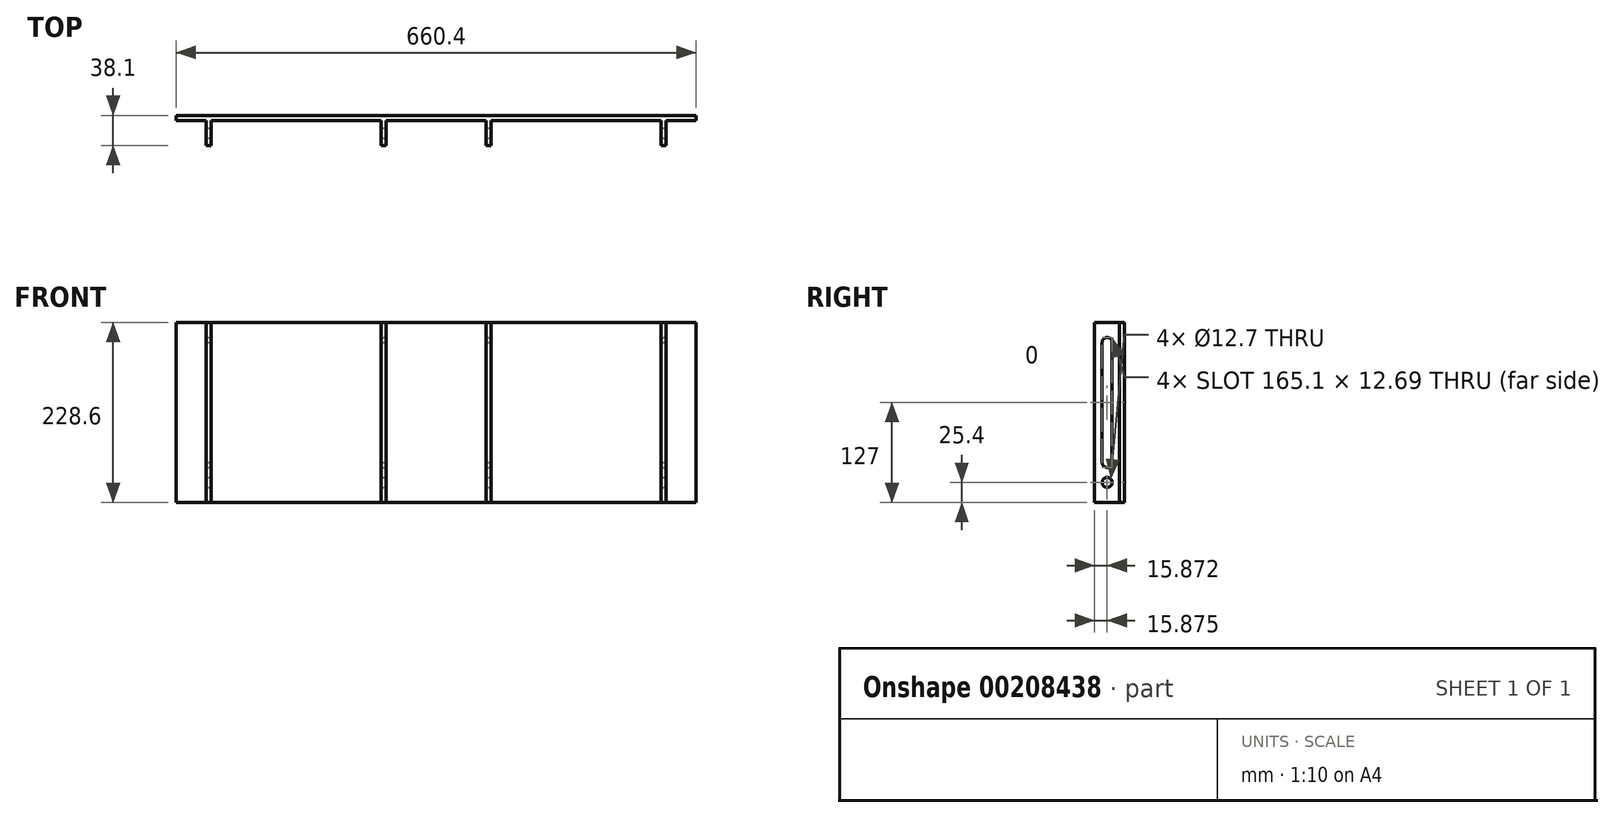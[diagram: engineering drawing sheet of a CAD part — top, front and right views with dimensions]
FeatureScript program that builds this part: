
annotation { "Feature Type Name" : "Feature", "Feature Type Description" : "" }
export const myFeature = defineFeature(function(context is Context, id is Id, definition is map)
    precondition{}
    {
        {
            var Q0;
            Q0=qCreatedBy(makeId("Front.planeOp"),FACE);
            var sketch = newSketch(context, id + "F0", { "sketchPlane" : qUnion([Q0])});
            skLineSegment(sketch, "E0.bottom", {"start": v(-330.2, 114.3) * mm, "end": v(330.2, 114.3) * mm});
            skLineSegment(sketch, "E0.top", {"start": v(-330.2, -114.3) * mm, "end": v(330.2, -114.3) * mm});
            skLineSegment(sketch, "E0.left", {"start": v(-330.2, 114.3) * mm, "end": v(-330.2, -114.3) * mm});
            skLineSegment(sketch, "E0.right", {"start": v(330.2, 114.3) * mm, "end": v(330.2, -114.3) * mm});
            skPoint(sketch, "E0.middle", {"position": v(0, 0) * mm});
            skLineSegment(sketch, "E1.bottom", {"start": v(-330.2, 114.3) * mm, "end": v(-292.1, 114.3) * mm});
            skLineSegment(sketch, "E1.top", {"start": v(-330.2, -114.3) * mm, "end": v(-292.1, -114.3) * mm});
            skLineSegment(sketch, "E2.bottom", {"start": v(330.2, 114.3) * mm, "end": v(292.1, 114.3) * mm});
            skLineSegment(sketch, "E2.top", {"start": v(330.2, -114.3) * mm, "end": v(292.1, -114.3) * mm});
            skLineSegment(sketch, "E3.bottom", {"start": v(-292.1, 114.3) * mm, "end": v(-285.75, 114.3) * mm});
            skLineSegment(sketch, "E3.top", {"start": v(-292.1, -114.3) * mm, "end": v(-285.75, -114.3) * mm});
            skLineSegment(sketch, "E4.bottom", {"start": v(292.1, 114.3) * mm, "end": v(285.75, 114.3) * mm});
            skLineSegment(sketch, "E4.top", {"start": v(292.1, -114.3) * mm, "end": v(285.75, -114.3) * mm});
            skSolve(sketch);
        }
        {
            var Q0;
            Q0=qSketchRegion(id+"F0",true);
            extrude(context, id + "F1", {"entities" : qUnion([Q0]), "depth" : 6.35 * mm});
        }
        {
            var Q0;
            Q0=makeQuery(id+"F1.opExtrude","CAP_FACE",FACE,{"disambiguationData":[OSD([sQuery(id+"F0.wireOp",EDGE,"E0.bottom"),sQuery(id+"F0.wireOp",EDGE,"E0.top"),sQuery(id+"F0.wireOp",EDGE,"E1.bottom"),sQuery(id+"F0.wireOp",EDGE,"E1.top"),sQuery(id+"F0.wireOp",EDGE,"E0.left"),sQuery(id+"F0.wireOp",EDGE,"E2.bottom"),sQuery(id+"F0.wireOp",EDGE,"E2.top"),sQuery(id+"F0.wireOp",EDGE,"E0.right"),sQuery(id+"F0.wireOp",EDGE,"E3.bottom"),sQuery(id+"F0.wireOp",EDGE,"E3.top"),sQuery(id+"F0.wireOp",EDGE,"E4.bottom"),sQuery(id+"F0.wireOp",EDGE,"E4.top")])],"isStart":false});
            var sketch = newSketch(context, id + "F2", { "sketchPlane" : qUnion([Q0])});
            skLineSegment(sketch, "E5.bottom", {"start": v(-330.2, 114.3) * mm, "end": v(-292.1, 114.3) * mm});
            skLineSegment(sketch, "E5.top", {"start": v(-330.2, -114.3) * mm, "end": v(-292.1, -114.3) * mm});
            skLineSegment(sketch, "E5.left", {"start": v(-330.2, 114.3) * mm, "end": v(-330.2, -114.3) * mm});
            skLineSegment(sketch, "E5.right", {"start": v(-292.1, 114.3) * mm, "end": v(-292.1, -114.3) * mm});
            skLineSegment(sketch, "E6.bottom", {"start": v(-292.1, 114.3) * mm, "end": v(-285.75, 114.3) * mm});
            skLineSegment(sketch, "E6.top", {"start": v(-292.1, -114.3) * mm, "end": v(-285.75, -114.3) * mm});
            skLineSegment(sketch, "E6.right", {"start": v(-285.75, 114.3) * mm, "end": v(-285.75, -114.3) * mm});
            skLineSegment(sketch, "E7.bottom", {"start": v(330.2, 114.3) * mm, "end": v(292.1, 114.3) * mm});
            skLineSegment(sketch, "E7.top", {"start": v(330.2, -114.3) * mm, "end": v(292.1, -114.3) * mm});
            skLineSegment(sketch, "E7.left", {"start": v(330.2, 114.3) * mm, "end": v(330.2, -114.3) * mm});
            skLineSegment(sketch, "E7.right", {"start": v(292.1, 114.3) * mm, "end": v(292.1, -114.3) * mm});
            skLineSegment(sketch, "E8.bottom", {"start": v(292.1, 114.3) * mm, "end": v(285.75, 114.3) * mm});
            skLineSegment(sketch, "E8.top", {"start": v(292.1, -114.3) * mm, "end": v(285.75, -114.3) * mm});
            skLineSegment(sketch, "E8.right", {"start": v(285.75, 114.3) * mm, "end": v(285.75, -114.3) * mm});
            skLineSegment(sketch, "E9.bottom", {"start": v(-285.75, 114.3) * mm, "end": v(-69.85, 114.3) * mm});
            skLineSegment(sketch, "E9.top", {"start": v(-285.75, -114.3) * mm, "end": v(-69.85, -114.3) * mm});
            skLineSegment(sketch, "E9.right", {"start": v(-69.85, 114.3) * mm, "end": v(-69.85, -114.3) * mm});
            skLineSegment(sketch, "E10.bottom", {"start": v(-69.85, 114.3) * mm, "end": v(-63.5, 114.3) * mm});
            skLineSegment(sketch, "E10.top", {"start": v(-69.85, -114.3) * mm, "end": v(-63.5, -114.3) * mm});
            skLineSegment(sketch, "E10.right", {"start": v(-63.5, 114.3) * mm, "end": v(-63.5, -114.3) * mm});
            skLineSegment(sketch, "E11.bottom", {"start": v(285.75, 114.3) * mm, "end": v(69.85, 114.3) * mm});
            skLineSegment(sketch, "E11.top", {"start": v(285.75, -114.3) * mm, "end": v(69.85, -114.3) * mm});
            skLineSegment(sketch, "E11.right", {"start": v(69.85, 114.3) * mm, "end": v(69.85, -114.3) * mm});
            skLineSegment(sketch, "E12.bottom", {"start": v(69.85, 114.3) * mm, "end": v(63.5, 114.3) * mm});
            skLineSegment(sketch, "E12.top", {"start": v(69.85, -114.3) * mm, "end": v(63.5, -114.3) * mm});
            skLineSegment(sketch, "E12.right", {"start": v(63.5, 114.3) * mm, "end": v(63.5, -114.3) * mm});
            skSolve(sketch);
        }
        {
            var Q0;
            Q0=makeQuery(id+"F2.imprint","IMPRINT",FACE,{"disambiguationData":[TD([[makeQuery(id+"F2.imprint","IMPRINT",EDGE,{"derivedFrom":sQuery(id+"F2.wireOp",EDGE,"E6.bottom")}),-1.0]])]});
            var Q1;
            Q1=makeQuery(id+"F2.imprint","IMPRINT",FACE,{"disambiguationData":[TD([[makeQuery(id+"F2.imprint","IMPRINT",EDGE,{"derivedFrom":sQuery(id+"F2.wireOp",EDGE,"E8.bottom")}),-1.0]])]});
            var Q2;
            Q2=makeQuery(id+"F2.imprint","IMPRINT",FACE,{"disambiguationData":[TD([[makeQuery(id+"F2.imprint","IMPRINT",EDGE,{"derivedFrom":sQuery(id+"F2.wireOp",EDGE,"E10.bottom")}),-1.0]])]});
            var Q3;
            Q3=makeQuery(id+"F2.imprint","IMPRINT",FACE,{"disambiguationData":[TD([[makeQuery(id+"F2.imprint","IMPRINT",EDGE,{"derivedFrom":sQuery(id+"F2.wireOp",EDGE,"E12.bottom")}),-1.0]])]});
            extrude(context, id + "F3", {"entities" : qUnion([Q0, Q1, Q2, Q3]), "operationType" : NewBodyOperationType.ADD, "depth" : 31.75 * mm});
        }
        {
            var Q0;
            Q0=makeQuery(id+"F3.opExtrude","SWEPT_FACE",FACE,{"disambiguationData":[OSD([sQuery(id+"F2.wireOp",EDGE,"E7.right")])]});
            var sketch = newSketch(context, id + "F4", { "sketchPlane" : qUnion([Q0])});
            skCircle(sketch, "E13", {"center": v(-22.23, -88.9) * mm, "radius": 6.35 * mm});
            skArc(sketch, "E14", {"start": v(-28.58, -63.5) * mm, "mid": v(-22.1, -69.85) * mm, "end": v(-15.88, -63.23) * mm});
            skArc(sketch, "E15", {"start": v(-15.88, 88.63) * mm, "mid": v(-22.1, 95.25) * mm, "end": v(-28.58, 88.9) * mm});
            skLineSegment(sketch, "E16", {"start": v(-28.58, -63.5) * mm, "end": v(-28.58, 88.9) * mm});
            skLineSegment(sketch, "E17", {"start": v(-15.88, -63.23) * mm, "end": v(-15.88, 89.17) * mm});
            skPoint(sketch, "E18.orphan", {"position": v(-22.23, -114.3) * mm});
            skPoint(sketch, "E19.start.orphan", {"position": v(-22.23, 114.3) * mm});
            skSolve(sketch);
        }
        {
            var Q0;
            Q0=qSketchRegion(id+"F4",true);
            extrude(context, id + "F5", {"entities" : qUnion([Q0]), "operationType" : NewBodyOperationType.REMOVE, "oppositeDirection" : true, "depth" : 762 * mm});
        }
    });
